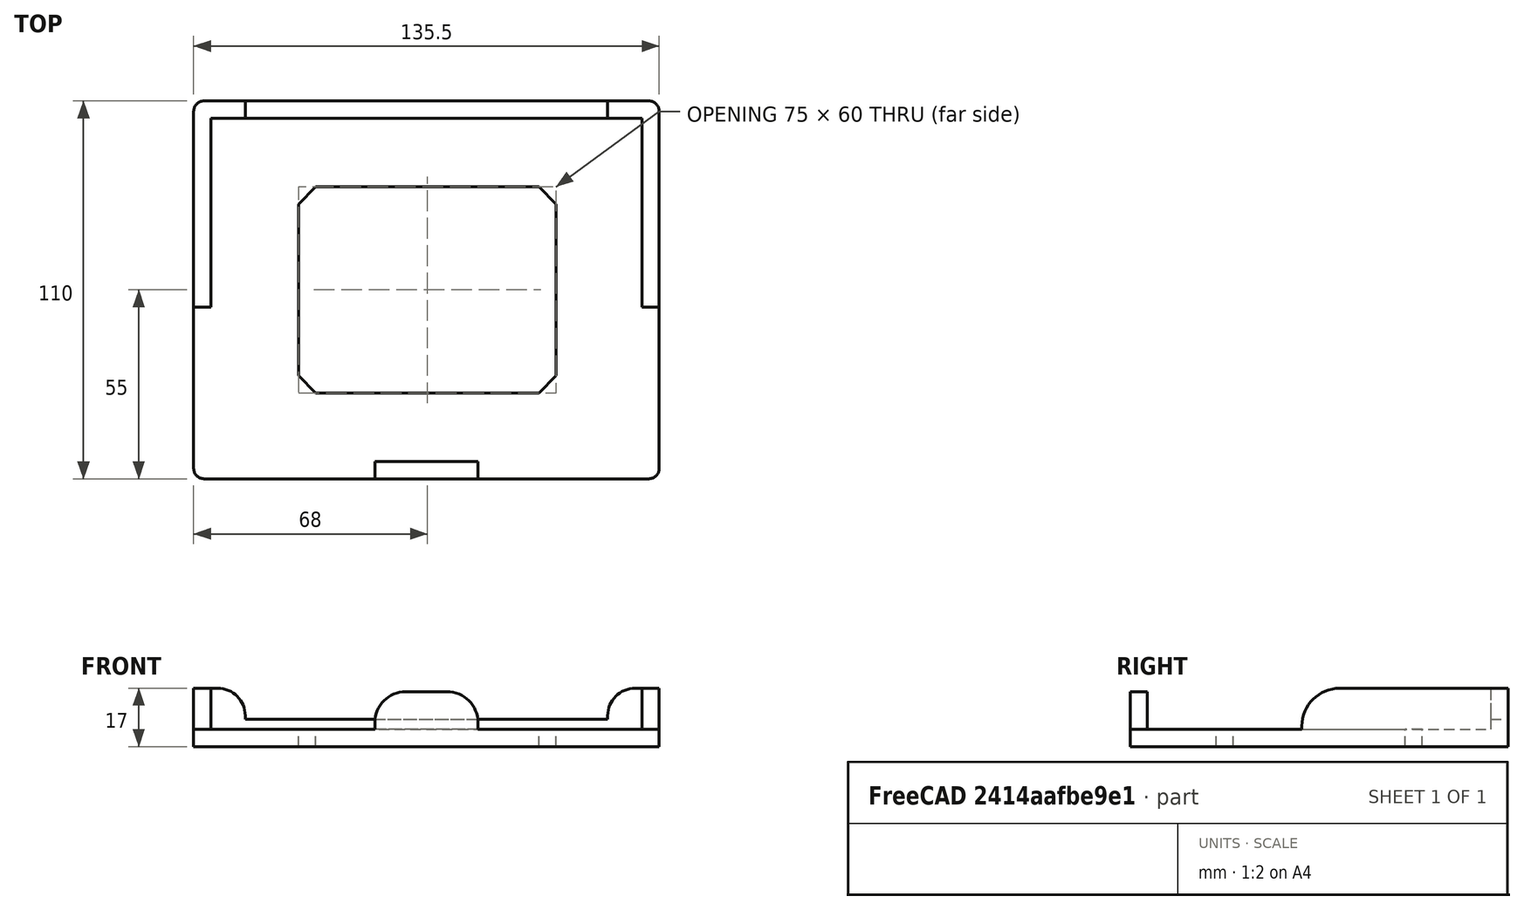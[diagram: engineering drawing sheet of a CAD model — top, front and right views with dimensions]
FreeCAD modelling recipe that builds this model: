
FCSTD DOCUMENT  (FreeCAD 0.14R3052 (Git))
Label: wdmount
License: CC-BY 3.0
LicenseURL: http://creativecommons.org/licenses/by/3.0/
objects: Part::Fillet×8, Part::Box×6, Part::Chamfer×4, Part::Cut×1, Part::MultiFuse×1
note: 20 computed .brp shape members not serialized (recipe doc carries the construction recipe); baked Part::Feature solids carry a one-line shape summary decoded from their .brp

FEATURE [Part::Box] Box
  Height = 5
  Length = 135.5
  Width = 110
FEATURE [Part::Fillet] Fillet
  Base = -> Box
  Edges = 4 edges r=3: [Edge1,Edge3,Edge5,Edge7]
FEATURE [Part::Box] Box001
  Height = 16
  Length = 30
  Placement = pos=(52.75,0,0) rot=(0,0,1;0rad)
  Width = 5
FEATURE [Part::Fillet] Fillet001  label="Front Retainer"
  Base = -> Box001
  Edges = 2 edges r=9: [Edge2,Edge6]
FEATURE [Part::Fillet] Fillet002
  Edges = 1 edges r=11: [Edge10]
FEATURE [Part::Fillet] Fillet003
  Base = -> Fillet002
  Edges = 1 edges r=3: [Edge5]
FEATURE [Part::Fillet] Fillet004
  Edges = 1 edges r=11: [Edge10]
  Placement = pos=(130.5,0,0) rot=(0,0,1;0rad)
FEATURE [Part::Fillet] Fillet005
  Base = -> Fillet004
  Edges = 1 edges r=3: [Edge15]
FEATURE [Part::Box] Box002
  Height = 17
  Length = 10
  Placement = pos=(5,105,0) rot=(0,0,1;0rad)
  Width = 5
FEATURE [Part::Fillet] Fillet006
  Base = -> Box002
  Edges = 1 edges r=8: [Edge6]
FEATURE [Part::Box] Box003
  Height = 17
  Length = 10
  Placement = pos=(120.5,105,0) rot=(0,0,1;0rad)
  Width = 5
FEATURE [Part::Fillet] Fillet007
  Base = -> Box003
  Edges = 1 edges r=8: [Edge2]
FEATURE [Part::Box] Box004
  Height = 8
  Length = 105.5
  Placement = pos=(15,105,0) rot=(0,0,1;0rad)
  Width = 5
FEATURE [Part::Box] Box005
  Height = 5
  Length = 75
  Placement = pos=(30.5,25,0) rot=(0,0,1;0rad)
  Width = 60
FEATURE [Part::Cut] Cut
  Base = -> Fillet
  Tool = -> Box005
FEATURE [Part::Chamfer] Chamfer
  Base = -> Cut
  Edges = 1 edges r=5: [Edge36]
FEATURE [Part::Chamfer] Chamfer001
  Base = -> Chamfer
  Edges = 1 edges r=5: [Edge22]
FEATURE [Part::Chamfer] Chamfer002
  Base = -> Chamfer001
  Edges = 1 edges r=5: [Edge24]
FEATURE [Part::Chamfer] Chamfer003
  Base = -> Chamfer002
  Edges = 1 edges r=5: [Edge24]
FEATURE [Part::MultiFuse] Fusion
  Shapes = -> [Chamfer003,Box004,Fillet007,Fillet006,Fillet005,Fillet003,Fillet001]
